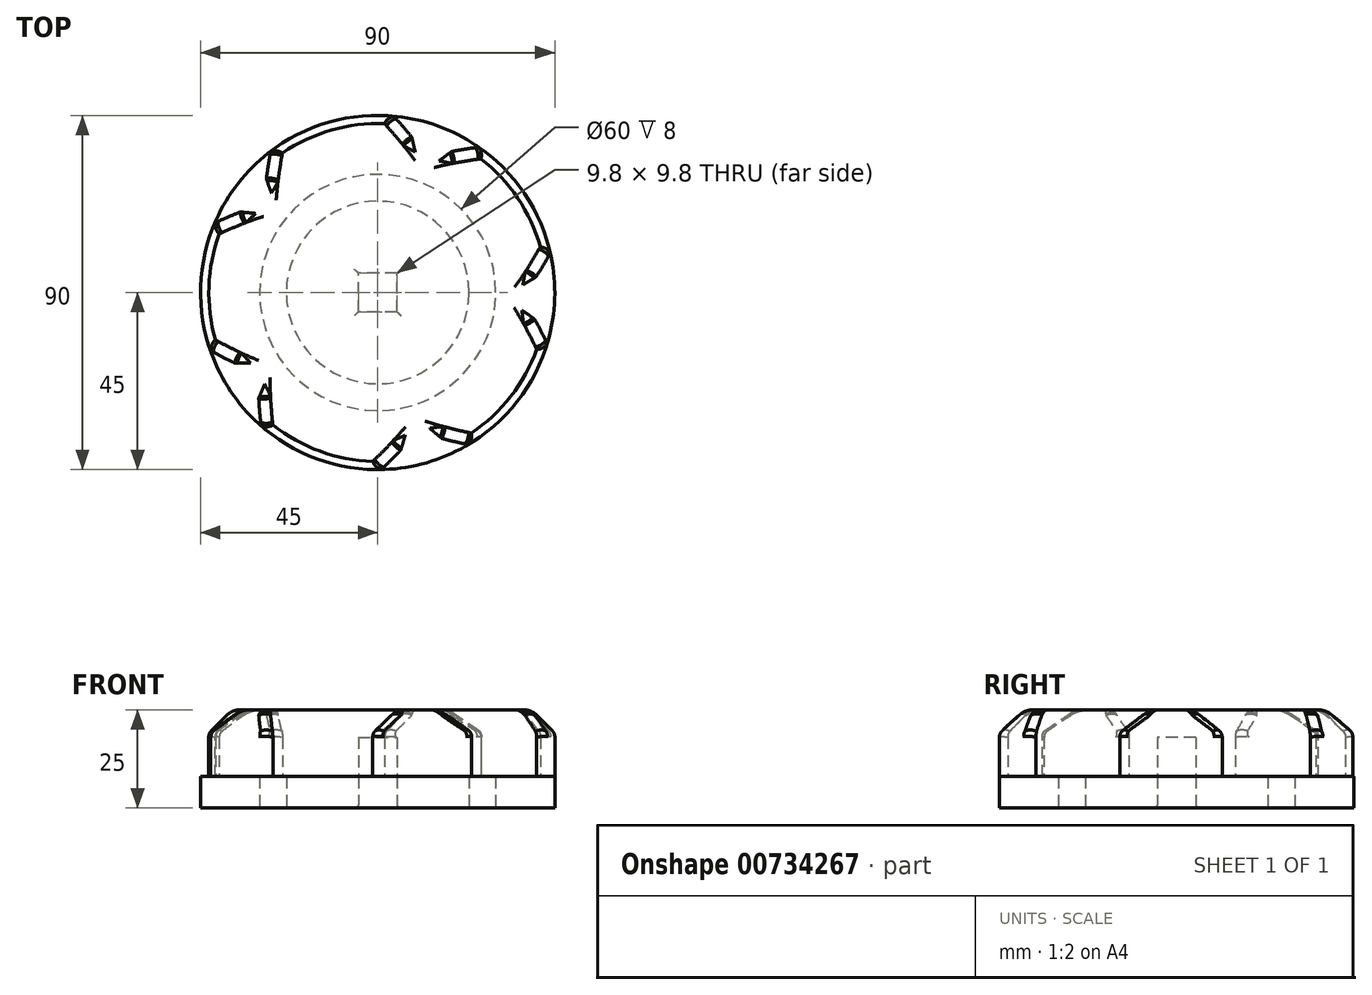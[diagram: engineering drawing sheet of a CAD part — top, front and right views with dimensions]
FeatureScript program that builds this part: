
annotation { "Feature Type Name" : "Feature", "Feature Type Description" : "" }
export const myFeature = defineFeature(function(context is Context, id is Id, definition is map)
    precondition{}
    {
        {
            var Q0;
            Q0=qCreatedBy(makeId("Top.planeOp"),FACE);
            var sketch = newSketch(context, id + "F0", { "sketchPlane" : qUnion([Q0])});
            skLineSegment(sketch, "E0.bottom", {"start": v(-4.9, 4.9) * mm, "end": v(4.9, 4.9) * mm});
            skLineSegment(sketch, "E0.top", {"start": v(-4.9, -4.9) * mm, "end": v(4.9, -4.9) * mm});
            skLineSegment(sketch, "E0.left", {"start": v(-4.9, 4.9) * mm, "end": v(-4.9, -4.9) * mm});
            skLineSegment(sketch, "E0.right", {"start": v(4.9, 4.9) * mm, "end": v(4.9, -4.9) * mm});
            skPoint(sketch, "E0.middle", {"position": v(0, 0) * mm});
            skCircle(sketch, "E1", {"center": v(0, 0) * mm, "radius": 23.2 * mm});
            skCircle(sketch, "E2", {"center": v(0, 0) * mm, "radius": 30 * mm});
            skCircle(sketch, "E3", {"center": v(0, 0) * mm, "radius": 45 * mm});
            skSolve(sketch);
        }
        {
            var Q0;
            Q0=makeQuery(id+"F0.imprint","IMPRINT",FACE,{"disambiguationData":[TD([[makeQuery(id+"F0.imprint","IMPRINT",EDGE,{"derivedFrom":sQuery(id+"F0.wireOp",EDGE,"E2")}),-1.0]])]});
            var Q1;
            Q1=makeQuery(id+"F0.imprint","IMPRINT",FACE,{"disambiguationData":[TD([[makeQuery(id+"F0.imprint","IMPRINT",EDGE,{"derivedFrom":sQuery(id+"F0.wireOp",EDGE,"E0.bottom")}),1.0]])]});
            extrude(context, id + "F1", {"entities" : qUnion([Q0, Q1]), "depth" : 8 * mm, "offsetDistance" : 25 * mm});
        }
        {
            var Q0;
            Q0=makeQuery(id+"F1.opExtrude","CAP_FACE",FACE,{"disambiguationData":[OSD([sQuery(id+"F0.wireOp",EDGE,"E2"),sQuery(id+"F0.wireOp",EDGE,"E3")])],"isStart":false});
            var sketch = newSketch(context, id + "F2", { "sketchPlane" : qUnion([Q0])});
            skArc(sketch, "E4", {"start": v(-42.2, 15.64) * mm, "mid": v(-44.97, 1.58) * mm, "end": v(-43.19, -12.65) * mm});
            skArc(sketch, "E5.1.1", {"start": v(-27.91, -35.3) * mm, "mid": v(-15.4, -42.28) * mm, "end": v(-1.32, -44.98) * mm});
            skArc(sketch, "E5.2.1", {"start": v(24.94, -37.45) * mm, "mid": v(35.46, -27.7) * mm, "end": v(42.37, -15.15) * mm});
            skArc(sketch, "E5.3.1", {"start": v(43.33, 12.15) * mm, "mid": v(37.3, 25.16) * mm, "end": v(27.5, 35.62) * mm});
            skArc(sketch, "E5.4.1", {"start": v(1.83, 44.96) * mm, "mid": v(-12.4, 43.26) * mm, "end": v(-25.37, 37.17) * mm});
            skCircle(sketch, "E6", {"center": v(0, 0) * mm, "radius": 45 * mm});
            skArc(sketch, "E7", {"start": v(-40.23, 14.91) * mm, "mid": v(-42.88, 1.5) * mm, "end": v(-41.18, -12.06) * mm});
            skLineSegment(sketch, "E8", {"start": v(-40.23, 14.91) * mm, "end": v(-42.2, 15.64) * mm});
            skLineSegment(sketch, "E9", {"start": v(-41.18, -12.06) * mm, "end": v(-43.19, -12.65) * mm});
            skLineSegment(sketch, "E10.1.0", {"start": v(-26.62, -33.66) * mm, "end": v(-27.91, -35.3) * mm});
            skArc(sketch, "E10.1.1", {"start": v(-26.62, -33.66) * mm, "mid": v(-14.68, -40.32) * mm, "end": v(-1.26, -42.9) * mm});
            skLineSegment(sketch, "E10.1.2", {"start": v(-1.26, -42.9) * mm, "end": v(-1.32, -44.98) * mm});
            skLineSegment(sketch, "E10.2.0", {"start": v(23.79, -35.71) * mm, "end": v(24.94, -37.45) * mm});
            skArc(sketch, "E10.2.1", {"start": v(23.79, -35.71) * mm, "mid": v(33.8, -26.42) * mm, "end": v(40.4, -14.45) * mm});
            skLineSegment(sketch, "E10.2.2", {"start": v(40.4, -14.45) * mm, "end": v(42.37, -15.15) * mm});
            skLineSegment(sketch, "E10.3.0", {"start": v(41.32, 11.58) * mm, "end": v(43.33, 12.15) * mm});
            skArc(sketch, "E10.3.1", {"start": v(41.32, 11.58) * mm, "mid": v(35.58, 23.99) * mm, "end": v(26.23, 33.96) * mm});
            skLineSegment(sketch, "E10.3.2", {"start": v(26.23, 33.96) * mm, "end": v(27.5, 35.62) * mm});
            skLineSegment(sketch, "E10.4.0", {"start": v(1.75, 42.87) * mm, "end": v(1.83, 44.96) * mm});
            skArc(sketch, "E10.4.1", {"start": v(1.75, 42.87) * mm, "mid": v(-11.82, 41.25) * mm, "end": v(-24.2, 35.44) * mm});
            skLineSegment(sketch, "E10.4.2", {"start": v(-24.2, 35.44) * mm, "end": v(-25.37, 37.17) * mm});
            skSolve(sketch);
        }
        {
            var Q0;
            Q0=makeQuery(id+"F2.imprint","IMPRINT",FACE,{"disambiguationData":[TD([[makeQuery(id+"F2.imprint","IMPRINT",EDGE,{"derivedFrom":sQuery(id+"F2.wireOp",EDGE,"E7")}),1.0]])]});
            var Q1;
            Q1=makeQuery(id+"F2.imprint","IMPRINT",FACE,{"disambiguationData":[TD([[makeQuery(id+"F2.imprint","IMPRINT",EDGE,{"derivedFrom":makeQuery(id+"F1.opExtrude","CAP_EDGE",EDGE,{"disambiguationData":[OSD([sQuery(id+"F0.wireOp",EDGE,"E2")])],"isStart":false})}),1.0]])]});
            extrude(context, id + "F3", {"entities" : qUnion([Q0, Q1]), "depth" : 17 * mm, "offsetDistance" : 25 * mm});
        }
        {
            var Q0;
            Q0=makeQuery(id+"F3.opExtrude","CAP_FACE",FACE,{"disambiguationData":[OSD([sQuery(id+"F2.wireOp",EDGE,"E6"),sQuery(id+"F2.wireOp",EDGE,"E7"),sQuery(id+"F2.wireOp",EDGE,"E8"),sQuery(id+"F2.wireOp",EDGE,"E9"),sQuery(id+"F2.wireOp",EDGE,"E10.1.0"),sQuery(id+"F2.wireOp",EDGE,"E10.1.1"),sQuery(id+"F2.wireOp",EDGE,"E10.1.2"),sQuery(id+"F2.wireOp",EDGE,"E10.2.0"),sQuery(id+"F2.wireOp",EDGE,"E10.2.1"),sQuery(id+"F2.wireOp",EDGE,"E10.2.2"),sQuery(id+"F2.wireOp",EDGE,"E10.3.0"),sQuery(id+"F2.wireOp",EDGE,"E10.3.1"),sQuery(id+"F2.wireOp",EDGE,"E10.3.2"),sQuery(id+"F2.wireOp",EDGE,"E10.4.0"),sQuery(id+"F2.wireOp",EDGE,"E10.4.1"),sQuery(id+"F2.wireOp",EDGE,"E10.4.2")])],"isStart":false});
            chamfer(context, id + "F4", {"entities" : qUnion([Q0]), "width" : 6 * mm, "tangentPropagation" : true});
        }
        {
            var Q0;
            Q0=makeQuery(id+"F3.opExtrude","CAP_FACE",FACE,{"disambiguationData":[OSD([sQuery(id+"F2.wireOp",EDGE,"E6"),sQuery(id+"F2.wireOp",EDGE,"E7"),sQuery(id+"F2.wireOp",EDGE,"E8"),sQuery(id+"F2.wireOp",EDGE,"E9"),sQuery(id+"F2.wireOp",EDGE,"E10.1.0"),sQuery(id+"F2.wireOp",EDGE,"E10.1.1"),sQuery(id+"F2.wireOp",EDGE,"E10.1.2"),sQuery(id+"F2.wireOp",EDGE,"E10.2.0"),sQuery(id+"F2.wireOp",EDGE,"E10.2.1"),sQuery(id+"F2.wireOp",EDGE,"E10.2.2"),sQuery(id+"F2.wireOp",EDGE,"E10.3.0"),sQuery(id+"F2.wireOp",EDGE,"E10.3.1"),sQuery(id+"F2.wireOp",EDGE,"E10.3.2"),sQuery(id+"F2.wireOp",EDGE,"E10.4.0"),sQuery(id+"F2.wireOp",EDGE,"E10.4.1"),sQuery(id+"F2.wireOp",EDGE,"E10.4.2")])],"isStart":false});
            fillet(context, id + "F5", {"entities" : qUnion([Q0]), "radius" : 5 * mm, "tangentPropagation" : true, "allowEdgeOverflow" : false});
        }
        {
            var Q0;
            Q0=makeQuery(id+"F3.opExtrude","SWEPT_EDGE",EDGE,{"disambiguationData":[OSD([sQuery(id+"F2.wireOp",EDGE,"E6"),sQuery(id+"F2.wireOp",EDGE,"E10.4.0")])]});
            var Q1;
            {var subQ0=sQuery(id+"F2.wireOp",EDGE,"E10.4.0");var subQ1=sQuery(id+"F2.wireOp",EDGE,"E6");Q1=makeQuery(id+"F4.opChamfer","BLEND_EDGE",EDGE,{"blendedFrom":[makeQuery(id+"F3.opExtrude","CAP_EDGE",EDGE,{"disambiguationData":[OSD([subQ1]),TDD([makeQuery(id+"F2.imprint","IMPRINT",EDGE,{"disambiguationData":[TD([[makeQuery(id+"F2.imprint","INTERSECT",VERTEX,{"derivedFrom":[subQ1,sQuery(id+"F2.wireOp",EDGE,"E10.3.2")]}),-1.0]])],"derivedFrom":subQ1})])],"isStart":false}),makeQuery(id+"F3.opExtrude","CAP_EDGE",EDGE,{"disambiguationData":[OSD([subQ0])],"isStart":false})],"blendedInto":[]});}
            var Q2;
            {var subQ0=sQuery(id+"F2.wireOp",EDGE,"E10.4.0");var subQ1=sQuery(id+"F2.wireOp",EDGE,"E10.3.2");var subQ2=sQuery(id+"F2.wireOp",EDGE,"E6");var subQ3=makeQuery(id+"F3.opExtrude","CAP_FACE",FACE,{"disambiguationData":[OSD([subQ2,sQuery(id+"F2.wireOp",EDGE,"E7"),sQuery(id+"F2.wireOp",EDGE,"E8"),sQuery(id+"F2.wireOp",EDGE,"E9"),sQuery(id+"F2.wireOp",EDGE,"E10.1.0"),sQuery(id+"F2.wireOp",EDGE,"E10.1.1"),sQuery(id+"F2.wireOp",EDGE,"E10.1.2"),sQuery(id+"F2.wireOp",EDGE,"E10.2.0"),sQuery(id+"F2.wireOp",EDGE,"E10.2.1"),sQuery(id+"F2.wireOp",EDGE,"E10.2.2"),sQuery(id+"F2.wireOp",EDGE,"E10.3.0"),sQuery(id+"F2.wireOp",EDGE,"E10.3.1"),subQ1,subQ0,sQuery(id+"F2.wireOp",EDGE,"E10.4.1"),sQuery(id+"F2.wireOp",EDGE,"E10.4.2")])],"isStart":false});Q2=makeQuery(id+"F5.opFillet","BLEND_EDGE",EDGE,{"blendedFrom":[makeQuery(id+"F4.opChamfer","BLEND_EDGE",EDGE,{"blendedFrom":[makeQuery(id+"F3.opExtrude","CAP_EDGE",EDGE,{"disambiguationData":[OSD([subQ2]),TDD([makeQuery(id+"F2.imprint","IMPRINT",EDGE,{"disambiguationData":[TD([[makeQuery(id+"F2.imprint","INTERSECT",VERTEX,{"derivedFrom":[subQ2,subQ1]}),-1.0]])],"derivedFrom":subQ2})])],"isStart":false}),subQ3],"blendedInto":[subQ3]}),makeQuery(id+"F4.opChamfer","BLEND_EDGE",EDGE,{"blendedFrom":[makeQuery(id+"F3.opExtrude","CAP_EDGE",EDGE,{"disambiguationData":[OSD([subQ0])],"isStart":false}),subQ3],"blendedInto":[subQ3]})],"blendedInto":[]});}
            var Q3;
            Q3=makeQuery(id+"F3.opExtrude","SWEPT_EDGE",EDGE,{"disambiguationData":[OSD([sQuery(id+"F2.wireOp",EDGE,"E6"),sQuery(id+"F2.wireOp",EDGE,"E10.4.2")])]});
            var Q4;
            {var subQ0=sQuery(id+"F2.wireOp",EDGE,"E10.4.2");var subQ1=sQuery(id+"F2.wireOp",EDGE,"E6");Q4=makeQuery(id+"F4.opChamfer","BLEND_EDGE",EDGE,{"blendedFrom":[makeQuery(id+"F3.opExtrude","CAP_EDGE",EDGE,{"disambiguationData":[OSD([subQ1]),TDD([makeQuery(id+"F2.imprint","IMPRINT",EDGE,{"disambiguationData":[TD([[makeQuery(id+"F2.imprint","INTERSECT",VERTEX,{"derivedFrom":[subQ1,sQuery(id+"F2.wireOp",EDGE,"E8")]}),1.0]])],"derivedFrom":subQ1})])],"isStart":false}),makeQuery(id+"F3.opExtrude","CAP_EDGE",EDGE,{"disambiguationData":[OSD([subQ0])],"isStart":false})],"blendedInto":[]});}
            var Q5;
            {var subQ0=sQuery(id+"F2.wireOp",EDGE,"E10.4.2");var subQ1=sQuery(id+"F2.wireOp",EDGE,"E8");var subQ2=sQuery(id+"F2.wireOp",EDGE,"E6");var subQ3=makeQuery(id+"F3.opExtrude","CAP_FACE",FACE,{"disambiguationData":[OSD([subQ2,sQuery(id+"F2.wireOp",EDGE,"E7"),subQ1,sQuery(id+"F2.wireOp",EDGE,"E9"),sQuery(id+"F2.wireOp",EDGE,"E10.1.0"),sQuery(id+"F2.wireOp",EDGE,"E10.1.1"),sQuery(id+"F2.wireOp",EDGE,"E10.1.2"),sQuery(id+"F2.wireOp",EDGE,"E10.2.0"),sQuery(id+"F2.wireOp",EDGE,"E10.2.1"),sQuery(id+"F2.wireOp",EDGE,"E10.2.2"),sQuery(id+"F2.wireOp",EDGE,"E10.3.0"),sQuery(id+"F2.wireOp",EDGE,"E10.3.1"),sQuery(id+"F2.wireOp",EDGE,"E10.3.2"),sQuery(id+"F2.wireOp",EDGE,"E10.4.0"),sQuery(id+"F2.wireOp",EDGE,"E10.4.1"),subQ0])],"isStart":false});Q5=makeQuery(id+"F5.opFillet","BLEND_EDGE",EDGE,{"blendedFrom":[makeQuery(id+"F4.opChamfer","BLEND_EDGE",EDGE,{"blendedFrom":[makeQuery(id+"F3.opExtrude","CAP_EDGE",EDGE,{"disambiguationData":[OSD([subQ2]),TDD([makeQuery(id+"F2.imprint","IMPRINT",EDGE,{"disambiguationData":[TD([[makeQuery(id+"F2.imprint","INTERSECT",VERTEX,{"derivedFrom":[subQ2,subQ1]}),1.0]])],"derivedFrom":subQ2})])],"isStart":false}),subQ3],"blendedInto":[subQ3]}),makeQuery(id+"F4.opChamfer","BLEND_EDGE",EDGE,{"blendedFrom":[makeQuery(id+"F3.opExtrude","CAP_EDGE",EDGE,{"disambiguationData":[OSD([subQ0])],"isStart":false}),subQ3],"blendedInto":[subQ3]})],"blendedInto":[]});}
            var Q6;
            Q6=makeQuery(id+"F3.opExtrude","SWEPT_EDGE",EDGE,{"disambiguationData":[OSD([sQuery(id+"F2.wireOp",EDGE,"E6"),sQuery(id+"F2.wireOp",EDGE,"E8")])]});
            var Q7;
            {var subQ0=sQuery(id+"F2.wireOp",EDGE,"E8");var subQ1=sQuery(id+"F2.wireOp",EDGE,"E6");Q7=makeQuery(id+"F4.opChamfer","BLEND_EDGE",EDGE,{"blendedFrom":[makeQuery(id+"F3.opExtrude","CAP_EDGE",EDGE,{"disambiguationData":[OSD([subQ1]),TDD([makeQuery(id+"F2.imprint","IMPRINT",EDGE,{"disambiguationData":[TD([[makeQuery(id+"F2.imprint","INTERSECT",VERTEX,{"derivedFrom":[subQ1,subQ0]}),1.0]])],"derivedFrom":subQ1})])],"isStart":false}),makeQuery(id+"F3.opExtrude","CAP_EDGE",EDGE,{"disambiguationData":[OSD([subQ0])],"isStart":false})],"blendedInto":[]});}
            var Q8;
            {var subQ0=sQuery(id+"F2.wireOp",EDGE,"E10.4.2");var subQ1=sQuery(id+"F2.wireOp",EDGE,"E8");var subQ2=sQuery(id+"F2.wireOp",EDGE,"E6");var subQ3=makeQuery(id+"F3.opExtrude","CAP_FACE",FACE,{"disambiguationData":[OSD([subQ2,sQuery(id+"F2.wireOp",EDGE,"E7"),subQ1,sQuery(id+"F2.wireOp",EDGE,"E9"),sQuery(id+"F2.wireOp",EDGE,"E10.1.0"),sQuery(id+"F2.wireOp",EDGE,"E10.1.1"),sQuery(id+"F2.wireOp",EDGE,"E10.1.2"),sQuery(id+"F2.wireOp",EDGE,"E10.2.0"),sQuery(id+"F2.wireOp",EDGE,"E10.2.1"),sQuery(id+"F2.wireOp",EDGE,"E10.2.2"),sQuery(id+"F2.wireOp",EDGE,"E10.3.0"),sQuery(id+"F2.wireOp",EDGE,"E10.3.1"),sQuery(id+"F2.wireOp",EDGE,"E10.3.2"),sQuery(id+"F2.wireOp",EDGE,"E10.4.0"),sQuery(id+"F2.wireOp",EDGE,"E10.4.1"),subQ0])],"isStart":false});Q8=makeQuery(id+"F5.opFillet","BLEND_EDGE",EDGE,{"blendedFrom":[makeQuery(id+"F4.opChamfer","BLEND_EDGE",EDGE,{"blendedFrom":[makeQuery(id+"F3.opExtrude","CAP_EDGE",EDGE,{"disambiguationData":[OSD([subQ2]),TDD([makeQuery(id+"F2.imprint","IMPRINT",EDGE,{"disambiguationData":[TD([[makeQuery(id+"F2.imprint","INTERSECT",VERTEX,{"derivedFrom":[subQ2,subQ1]}),1.0]])],"derivedFrom":subQ2})])],"isStart":false}),subQ3],"blendedInto":[subQ3]}),makeQuery(id+"F4.opChamfer","BLEND_EDGE",EDGE,{"blendedFrom":[makeQuery(id+"F3.opExtrude","CAP_EDGE",EDGE,{"disambiguationData":[OSD([subQ1])],"isStart":false}),subQ3],"blendedInto":[subQ3]})],"blendedInto":[]});}
            var Q9;
            {var subQ0=sQuery(id+"F2.wireOp",EDGE,"E9");var subQ1=sQuery(id+"F2.wireOp",EDGE,"E6");Q9=makeQuery(id+"F4.opChamfer","BLEND_EDGE",EDGE,{"blendedFrom":[makeQuery(id+"F3.opExtrude","CAP_EDGE",EDGE,{"disambiguationData":[OSD([subQ1]),TDD([makeQuery(id+"F2.imprint","IMPRINT",EDGE,{"disambiguationData":[TD([[makeQuery(id+"F2.imprint","INTERSECT",VERTEX,{"derivedFrom":[subQ1,subQ0]}),-1.0]])],"derivedFrom":subQ1})])],"isStart":false}),makeQuery(id+"F3.opExtrude","CAP_EDGE",EDGE,{"disambiguationData":[OSD([subQ0])],"isStart":false})],"blendedInto":[]});}
            var Q10;
            Q10=makeQuery(id+"F3.opExtrude","SWEPT_EDGE",EDGE,{"disambiguationData":[OSD([sQuery(id+"F2.wireOp",EDGE,"E6"),sQuery(id+"F2.wireOp",EDGE,"E9")])]});
            var Q11;
            {var subQ0=sQuery(id+"F2.wireOp",EDGE,"E10.1.0");var subQ1=sQuery(id+"F2.wireOp",EDGE,"E9");var subQ2=sQuery(id+"F2.wireOp",EDGE,"E6");var subQ3=makeQuery(id+"F3.opExtrude","CAP_FACE",FACE,{"disambiguationData":[OSD([subQ2,sQuery(id+"F2.wireOp",EDGE,"E7"),sQuery(id+"F2.wireOp",EDGE,"E8"),subQ1,subQ0,sQuery(id+"F2.wireOp",EDGE,"E10.1.1"),sQuery(id+"F2.wireOp",EDGE,"E10.1.2"),sQuery(id+"F2.wireOp",EDGE,"E10.2.0"),sQuery(id+"F2.wireOp",EDGE,"E10.2.1"),sQuery(id+"F2.wireOp",EDGE,"E10.2.2"),sQuery(id+"F2.wireOp",EDGE,"E10.3.0"),sQuery(id+"F2.wireOp",EDGE,"E10.3.1"),sQuery(id+"F2.wireOp",EDGE,"E10.3.2"),sQuery(id+"F2.wireOp",EDGE,"E10.4.0"),sQuery(id+"F2.wireOp",EDGE,"E10.4.1"),sQuery(id+"F2.wireOp",EDGE,"E10.4.2")])],"isStart":false});Q11=makeQuery(id+"F5.opFillet","BLEND_EDGE",EDGE,{"blendedFrom":[makeQuery(id+"F4.opChamfer","BLEND_EDGE",EDGE,{"blendedFrom":[makeQuery(id+"F3.opExtrude","CAP_EDGE",EDGE,{"disambiguationData":[OSD([subQ2]),TDD([makeQuery(id+"F2.imprint","IMPRINT",EDGE,{"disambiguationData":[TD([[makeQuery(id+"F2.imprint","INTERSECT",VERTEX,{"derivedFrom":[subQ2,subQ1]}),-1.0]])],"derivedFrom":subQ2})])],"isStart":false}),subQ3],"blendedInto":[subQ3]}),makeQuery(id+"F4.opChamfer","BLEND_EDGE",EDGE,{"blendedFrom":[makeQuery(id+"F3.opExtrude","CAP_EDGE",EDGE,{"disambiguationData":[OSD([subQ1])],"isStart":false}),subQ3],"blendedInto":[subQ3]})],"blendedInto":[]});}
            var Q12;
            {var subQ0=sQuery(id+"F2.wireOp",EDGE,"E10.1.0");var subQ1=sQuery(id+"F2.wireOp",EDGE,"E9");var subQ2=sQuery(id+"F2.wireOp",EDGE,"E6");var subQ3=makeQuery(id+"F3.opExtrude","CAP_FACE",FACE,{"disambiguationData":[OSD([subQ2,sQuery(id+"F2.wireOp",EDGE,"E7"),sQuery(id+"F2.wireOp",EDGE,"E8"),subQ1,subQ0,sQuery(id+"F2.wireOp",EDGE,"E10.1.1"),sQuery(id+"F2.wireOp",EDGE,"E10.1.2"),sQuery(id+"F2.wireOp",EDGE,"E10.2.0"),sQuery(id+"F2.wireOp",EDGE,"E10.2.1"),sQuery(id+"F2.wireOp",EDGE,"E10.2.2"),sQuery(id+"F2.wireOp",EDGE,"E10.3.0"),sQuery(id+"F2.wireOp",EDGE,"E10.3.1"),sQuery(id+"F2.wireOp",EDGE,"E10.3.2"),sQuery(id+"F2.wireOp",EDGE,"E10.4.0"),sQuery(id+"F2.wireOp",EDGE,"E10.4.1"),sQuery(id+"F2.wireOp",EDGE,"E10.4.2")])],"isStart":false});Q12=makeQuery(id+"F5.opFillet","BLEND_EDGE",EDGE,{"blendedFrom":[makeQuery(id+"F4.opChamfer","BLEND_EDGE",EDGE,{"blendedFrom":[makeQuery(id+"F3.opExtrude","CAP_EDGE",EDGE,{"disambiguationData":[OSD([subQ2]),TDD([makeQuery(id+"F2.imprint","IMPRINT",EDGE,{"disambiguationData":[TD([[makeQuery(id+"F2.imprint","INTERSECT",VERTEX,{"derivedFrom":[subQ2,subQ1]}),-1.0]])],"derivedFrom":subQ2})])],"isStart":false}),subQ3],"blendedInto":[subQ3]}),makeQuery(id+"F4.opChamfer","BLEND_EDGE",EDGE,{"blendedFrom":[makeQuery(id+"F3.opExtrude","CAP_EDGE",EDGE,{"disambiguationData":[OSD([subQ0])],"isStart":false}),subQ3],"blendedInto":[subQ3]})],"blendedInto":[]});}
            var Q13;
            {var subQ0=sQuery(id+"F2.wireOp",EDGE,"E10.1.0");var subQ1=sQuery(id+"F2.wireOp",EDGE,"E6");Q13=makeQuery(id+"F4.opChamfer","BLEND_EDGE",EDGE,{"blendedFrom":[makeQuery(id+"F3.opExtrude","CAP_EDGE",EDGE,{"disambiguationData":[OSD([subQ1]),TDD([makeQuery(id+"F2.imprint","IMPRINT",EDGE,{"disambiguationData":[TD([[makeQuery(id+"F2.imprint","INTERSECT",VERTEX,{"derivedFrom":[subQ1,sQuery(id+"F2.wireOp",EDGE,"E9")]}),-1.0]])],"derivedFrom":subQ1})])],"isStart":false}),makeQuery(id+"F3.opExtrude","CAP_EDGE",EDGE,{"disambiguationData":[OSD([subQ0])],"isStart":false})],"blendedInto":[]});}
            var Q14;
            Q14=makeQuery(id+"F3.opExtrude","SWEPT_EDGE",EDGE,{"disambiguationData":[OSD([sQuery(id+"F2.wireOp",EDGE,"E6"),sQuery(id+"F2.wireOp",EDGE,"E10.1.0")])]});
            var Q15;
            Q15=makeQuery(id+"F3.opExtrude","SWEPT_EDGE",EDGE,{"disambiguationData":[OSD([sQuery(id+"F2.wireOp",EDGE,"E6"),sQuery(id+"F2.wireOp",EDGE,"E10.1.2")])]});
            var Q16;
            {var subQ0=sQuery(id+"F2.wireOp",EDGE,"E10.1.2");var subQ1=sQuery(id+"F2.wireOp",EDGE,"E6");Q16=makeQuery(id+"F4.opChamfer","BLEND_EDGE",EDGE,{"blendedFrom":[makeQuery(id+"F3.opExtrude","CAP_EDGE",EDGE,{"disambiguationData":[OSD([subQ1]),TDD([makeQuery(id+"F2.imprint","IMPRINT",EDGE,{"disambiguationData":[TD([[makeQuery(id+"F2.imprint","INTERSECT",VERTEX,{"derivedFrom":[subQ1,subQ0]}),-1.0]])],"derivedFrom":subQ1})])],"isStart":false}),makeQuery(id+"F3.opExtrude","CAP_EDGE",EDGE,{"disambiguationData":[OSD([subQ0])],"isStart":false})],"blendedInto":[]});}
            var Q17;
            {var subQ0=sQuery(id+"F2.wireOp",EDGE,"E10.2.0");var subQ1=sQuery(id+"F2.wireOp",EDGE,"E10.1.2");var subQ2=sQuery(id+"F2.wireOp",EDGE,"E6");var subQ3=makeQuery(id+"F3.opExtrude","CAP_FACE",FACE,{"disambiguationData":[OSD([subQ2,sQuery(id+"F2.wireOp",EDGE,"E7"),sQuery(id+"F2.wireOp",EDGE,"E8"),sQuery(id+"F2.wireOp",EDGE,"E9"),sQuery(id+"F2.wireOp",EDGE,"E10.1.0"),sQuery(id+"F2.wireOp",EDGE,"E10.1.1"),subQ1,subQ0,sQuery(id+"F2.wireOp",EDGE,"E10.2.1"),sQuery(id+"F2.wireOp",EDGE,"E10.2.2"),sQuery(id+"F2.wireOp",EDGE,"E10.3.0"),sQuery(id+"F2.wireOp",EDGE,"E10.3.1"),sQuery(id+"F2.wireOp",EDGE,"E10.3.2"),sQuery(id+"F2.wireOp",EDGE,"E10.4.0"),sQuery(id+"F2.wireOp",EDGE,"E10.4.1"),sQuery(id+"F2.wireOp",EDGE,"E10.4.2")])],"isStart":false});Q17=makeQuery(id+"F5.opFillet","BLEND_EDGE",EDGE,{"blendedFrom":[makeQuery(id+"F4.opChamfer","BLEND_EDGE",EDGE,{"blendedFrom":[makeQuery(id+"F3.opExtrude","CAP_EDGE",EDGE,{"disambiguationData":[OSD([subQ2]),TDD([makeQuery(id+"F2.imprint","IMPRINT",EDGE,{"disambiguationData":[TD([[makeQuery(id+"F2.imprint","INTERSECT",VERTEX,{"derivedFrom":[subQ2,subQ1]}),-1.0]])],"derivedFrom":subQ2})])],"isStart":false}),subQ3],"blendedInto":[subQ3]}),makeQuery(id+"F4.opChamfer","BLEND_EDGE",EDGE,{"blendedFrom":[makeQuery(id+"F3.opExtrude","CAP_EDGE",EDGE,{"disambiguationData":[OSD([subQ1])],"isStart":false}),subQ3],"blendedInto":[subQ3]})],"blendedInto":[]});}
            var Q18;
            {var subQ0=sQuery(id+"F2.wireOp",EDGE,"E10.2.0");var subQ1=sQuery(id+"F2.wireOp",EDGE,"E10.1.2");var subQ2=sQuery(id+"F2.wireOp",EDGE,"E6");var subQ3=makeQuery(id+"F3.opExtrude","CAP_FACE",FACE,{"disambiguationData":[OSD([subQ2,sQuery(id+"F2.wireOp",EDGE,"E7"),sQuery(id+"F2.wireOp",EDGE,"E8"),sQuery(id+"F2.wireOp",EDGE,"E9"),sQuery(id+"F2.wireOp",EDGE,"E10.1.0"),sQuery(id+"F2.wireOp",EDGE,"E10.1.1"),subQ1,subQ0,sQuery(id+"F2.wireOp",EDGE,"E10.2.1"),sQuery(id+"F2.wireOp",EDGE,"E10.2.2"),sQuery(id+"F2.wireOp",EDGE,"E10.3.0"),sQuery(id+"F2.wireOp",EDGE,"E10.3.1"),sQuery(id+"F2.wireOp",EDGE,"E10.3.2"),sQuery(id+"F2.wireOp",EDGE,"E10.4.0"),sQuery(id+"F2.wireOp",EDGE,"E10.4.1"),sQuery(id+"F2.wireOp",EDGE,"E10.4.2")])],"isStart":false});Q18=makeQuery(id+"F5.opFillet","BLEND_EDGE",EDGE,{"blendedFrom":[makeQuery(id+"F4.opChamfer","BLEND_EDGE",EDGE,{"blendedFrom":[makeQuery(id+"F3.opExtrude","CAP_EDGE",EDGE,{"disambiguationData":[OSD([subQ2]),TDD([makeQuery(id+"F2.imprint","IMPRINT",EDGE,{"disambiguationData":[TD([[makeQuery(id+"F2.imprint","INTERSECT",VERTEX,{"derivedFrom":[subQ2,subQ1]}),-1.0]])],"derivedFrom":subQ2})])],"isStart":false}),subQ3],"blendedInto":[subQ3]}),makeQuery(id+"F4.opChamfer","BLEND_EDGE",EDGE,{"blendedFrom":[makeQuery(id+"F3.opExtrude","CAP_EDGE",EDGE,{"disambiguationData":[OSD([subQ0])],"isStart":false}),subQ3],"blendedInto":[subQ3]})],"blendedInto":[]});}
            var Q19;
            {var subQ0=sQuery(id+"F2.wireOp",EDGE,"E10.2.0");var subQ1=sQuery(id+"F2.wireOp",EDGE,"E6");Q19=makeQuery(id+"F4.opChamfer","BLEND_EDGE",EDGE,{"blendedFrom":[makeQuery(id+"F3.opExtrude","CAP_EDGE",EDGE,{"disambiguationData":[OSD([subQ1]),TDD([makeQuery(id+"F2.imprint","IMPRINT",EDGE,{"disambiguationData":[TD([[makeQuery(id+"F2.imprint","INTERSECT",VERTEX,{"derivedFrom":[subQ1,sQuery(id+"F2.wireOp",EDGE,"E10.1.2")]}),-1.0]])],"derivedFrom":subQ1})])],"isStart":false}),makeQuery(id+"F3.opExtrude","CAP_EDGE",EDGE,{"disambiguationData":[OSD([subQ0])],"isStart":false})],"blendedInto":[]});}
            var Q20;
            Q20=makeQuery(id+"F3.opExtrude","SWEPT_EDGE",EDGE,{"disambiguationData":[OSD([sQuery(id+"F2.wireOp",EDGE,"E6"),sQuery(id+"F2.wireOp",EDGE,"E10.2.0")])]});
            var Q21;
            Q21=makeQuery(id+"F3.opExtrude","SWEPT_EDGE",EDGE,{"disambiguationData":[OSD([sQuery(id+"F2.wireOp",EDGE,"E6"),sQuery(id+"F2.wireOp",EDGE,"E10.2.2")])]});
            var Q22;
            {var subQ0=sQuery(id+"F2.wireOp",EDGE,"E10.2.2");var subQ1=sQuery(id+"F2.wireOp",EDGE,"E6");Q22=makeQuery(id+"F4.opChamfer","BLEND_EDGE",EDGE,{"blendedFrom":[makeQuery(id+"F3.opExtrude","CAP_EDGE",EDGE,{"disambiguationData":[OSD([subQ1]),TDD([makeQuery(id+"F2.imprint","IMPRINT",EDGE,{"disambiguationData":[TD([[makeQuery(id+"F2.imprint","INTERSECT",VERTEX,{"derivedFrom":[subQ1,subQ0]}),-1.0]])],"derivedFrom":subQ1})])],"isStart":false}),makeQuery(id+"F3.opExtrude","CAP_EDGE",EDGE,{"disambiguationData":[OSD([subQ0])],"isStart":false})],"blendedInto":[]});}
            var Q23;
            {var subQ0=sQuery(id+"F2.wireOp",EDGE,"E10.3.0");var subQ1=sQuery(id+"F2.wireOp",EDGE,"E10.2.2");var subQ2=sQuery(id+"F2.wireOp",EDGE,"E6");var subQ3=makeQuery(id+"F3.opExtrude","CAP_FACE",FACE,{"disambiguationData":[OSD([subQ2,sQuery(id+"F2.wireOp",EDGE,"E7"),sQuery(id+"F2.wireOp",EDGE,"E8"),sQuery(id+"F2.wireOp",EDGE,"E9"),sQuery(id+"F2.wireOp",EDGE,"E10.1.0"),sQuery(id+"F2.wireOp",EDGE,"E10.1.1"),sQuery(id+"F2.wireOp",EDGE,"E10.1.2"),sQuery(id+"F2.wireOp",EDGE,"E10.2.0"),sQuery(id+"F2.wireOp",EDGE,"E10.2.1"),subQ1,subQ0,sQuery(id+"F2.wireOp",EDGE,"E10.3.1"),sQuery(id+"F2.wireOp",EDGE,"E10.3.2"),sQuery(id+"F2.wireOp",EDGE,"E10.4.0"),sQuery(id+"F2.wireOp",EDGE,"E10.4.1"),sQuery(id+"F2.wireOp",EDGE,"E10.4.2")])],"isStart":false});Q23=makeQuery(id+"F5.opFillet","BLEND_EDGE",EDGE,{"blendedFrom":[makeQuery(id+"F4.opChamfer","BLEND_EDGE",EDGE,{"blendedFrom":[makeQuery(id+"F3.opExtrude","CAP_EDGE",EDGE,{"disambiguationData":[OSD([subQ2]),TDD([makeQuery(id+"F2.imprint","IMPRINT",EDGE,{"disambiguationData":[TD([[makeQuery(id+"F2.imprint","INTERSECT",VERTEX,{"derivedFrom":[subQ2,subQ1]}),-1.0]])],"derivedFrom":subQ2})])],"isStart":false}),subQ3],"blendedInto":[subQ3]}),makeQuery(id+"F4.opChamfer","BLEND_EDGE",EDGE,{"blendedFrom":[makeQuery(id+"F3.opExtrude","CAP_EDGE",EDGE,{"disambiguationData":[OSD([subQ1])],"isStart":false}),subQ3],"blendedInto":[subQ3]})],"blendedInto":[]});}
            var Q24;
            Q24=makeQuery(id+"F3.opExtrude","SWEPT_EDGE",EDGE,{"disambiguationData":[OSD([sQuery(id+"F2.wireOp",EDGE,"E6"),sQuery(id+"F2.wireOp",EDGE,"E10.3.0")])]});
            var Q25;
            {var subQ0=sQuery(id+"F2.wireOp",EDGE,"E10.3.0");var subQ1=sQuery(id+"F2.wireOp",EDGE,"E6");Q25=makeQuery(id+"F4.opChamfer","BLEND_EDGE",EDGE,{"blendedFrom":[makeQuery(id+"F3.opExtrude","CAP_EDGE",EDGE,{"disambiguationData":[OSD([subQ1]),TDD([makeQuery(id+"F2.imprint","IMPRINT",EDGE,{"disambiguationData":[TD([[makeQuery(id+"F2.imprint","INTERSECT",VERTEX,{"derivedFrom":[subQ1,sQuery(id+"F2.wireOp",EDGE,"E10.2.2")]}),-1.0]])],"derivedFrom":subQ1})])],"isStart":false}),makeQuery(id+"F3.opExtrude","CAP_EDGE",EDGE,{"disambiguationData":[OSD([subQ0])],"isStart":false})],"blendedInto":[]});}
            var Q26;
            {var subQ0=sQuery(id+"F2.wireOp",EDGE,"E10.3.0");var subQ1=sQuery(id+"F2.wireOp",EDGE,"E10.2.2");var subQ2=sQuery(id+"F2.wireOp",EDGE,"E6");var subQ3=makeQuery(id+"F3.opExtrude","CAP_FACE",FACE,{"disambiguationData":[OSD([subQ2,sQuery(id+"F2.wireOp",EDGE,"E7"),sQuery(id+"F2.wireOp",EDGE,"E8"),sQuery(id+"F2.wireOp",EDGE,"E9"),sQuery(id+"F2.wireOp",EDGE,"E10.1.0"),sQuery(id+"F2.wireOp",EDGE,"E10.1.1"),sQuery(id+"F2.wireOp",EDGE,"E10.1.2"),sQuery(id+"F2.wireOp",EDGE,"E10.2.0"),sQuery(id+"F2.wireOp",EDGE,"E10.2.1"),subQ1,subQ0,sQuery(id+"F2.wireOp",EDGE,"E10.3.1"),sQuery(id+"F2.wireOp",EDGE,"E10.3.2"),sQuery(id+"F2.wireOp",EDGE,"E10.4.0"),sQuery(id+"F2.wireOp",EDGE,"E10.4.1"),sQuery(id+"F2.wireOp",EDGE,"E10.4.2")])],"isStart":false});Q26=makeQuery(id+"F5.opFillet","BLEND_EDGE",EDGE,{"blendedFrom":[makeQuery(id+"F4.opChamfer","BLEND_EDGE",EDGE,{"blendedFrom":[makeQuery(id+"F3.opExtrude","CAP_EDGE",EDGE,{"disambiguationData":[OSD([subQ2]),TDD([makeQuery(id+"F2.imprint","IMPRINT",EDGE,{"disambiguationData":[TD([[makeQuery(id+"F2.imprint","INTERSECT",VERTEX,{"derivedFrom":[subQ2,subQ1]}),-1.0]])],"derivedFrom":subQ2})])],"isStart":false}),subQ3],"blendedInto":[subQ3]}),makeQuery(id+"F4.opChamfer","BLEND_EDGE",EDGE,{"blendedFrom":[makeQuery(id+"F3.opExtrude","CAP_EDGE",EDGE,{"disambiguationData":[OSD([subQ0])],"isStart":false}),subQ3],"blendedInto":[subQ3]})],"blendedInto":[]});}
            var Q27;
            Q27=makeQuery(id+"F3.opExtrude","SWEPT_EDGE",EDGE,{"disambiguationData":[OSD([sQuery(id+"F2.wireOp",EDGE,"E6"),sQuery(id+"F2.wireOp",EDGE,"E10.3.2")])]});
            var Q28;
            {var subQ0=sQuery(id+"F2.wireOp",EDGE,"E10.3.2");var subQ1=sQuery(id+"F2.wireOp",EDGE,"E6");Q28=makeQuery(id+"F4.opChamfer","BLEND_EDGE",EDGE,{"blendedFrom":[makeQuery(id+"F3.opExtrude","CAP_EDGE",EDGE,{"disambiguationData":[OSD([subQ1]),TDD([makeQuery(id+"F2.imprint","IMPRINT",EDGE,{"disambiguationData":[TD([[makeQuery(id+"F2.imprint","INTERSECT",VERTEX,{"derivedFrom":[subQ1,subQ0]}),-1.0]])],"derivedFrom":subQ1})])],"isStart":false}),makeQuery(id+"F3.opExtrude","CAP_EDGE",EDGE,{"disambiguationData":[OSD([subQ0])],"isStart":false})],"blendedInto":[]});}
            var Q29;
            {var subQ0=sQuery(id+"F2.wireOp",EDGE,"E10.4.0");var subQ1=sQuery(id+"F2.wireOp",EDGE,"E10.3.2");var subQ2=sQuery(id+"F2.wireOp",EDGE,"E6");var subQ3=makeQuery(id+"F3.opExtrude","CAP_FACE",FACE,{"disambiguationData":[OSD([subQ2,sQuery(id+"F2.wireOp",EDGE,"E7"),sQuery(id+"F2.wireOp",EDGE,"E8"),sQuery(id+"F2.wireOp",EDGE,"E9"),sQuery(id+"F2.wireOp",EDGE,"E10.1.0"),sQuery(id+"F2.wireOp",EDGE,"E10.1.1"),sQuery(id+"F2.wireOp",EDGE,"E10.1.2"),sQuery(id+"F2.wireOp",EDGE,"E10.2.0"),sQuery(id+"F2.wireOp",EDGE,"E10.2.1"),sQuery(id+"F2.wireOp",EDGE,"E10.2.2"),sQuery(id+"F2.wireOp",EDGE,"E10.3.0"),sQuery(id+"F2.wireOp",EDGE,"E10.3.1"),subQ1,subQ0,sQuery(id+"F2.wireOp",EDGE,"E10.4.1"),sQuery(id+"F2.wireOp",EDGE,"E10.4.2")])],"isStart":false});Q29=makeQuery(id+"F5.opFillet","BLEND_EDGE",EDGE,{"blendedFrom":[makeQuery(id+"F4.opChamfer","BLEND_EDGE",EDGE,{"blendedFrom":[makeQuery(id+"F3.opExtrude","CAP_EDGE",EDGE,{"disambiguationData":[OSD([subQ2]),TDD([makeQuery(id+"F2.imprint","IMPRINT",EDGE,{"disambiguationData":[TD([[makeQuery(id+"F2.imprint","INTERSECT",VERTEX,{"derivedFrom":[subQ2,subQ1]}),-1.0]])],"derivedFrom":subQ2})])],"isStart":false}),subQ3],"blendedInto":[subQ3]}),makeQuery(id+"F4.opChamfer","BLEND_EDGE",EDGE,{"blendedFrom":[makeQuery(id+"F3.opExtrude","CAP_EDGE",EDGE,{"disambiguationData":[OSD([subQ1])],"isStart":false}),subQ3],"blendedInto":[subQ3]})],"blendedInto":[]});}
            fillet(context, id + "F6", {"entities" : qUnion([Q0, Q1, Q2, Q3, Q4, Q5, Q6, Q7, Q8, Q9, Q10, Q11, Q12, Q13, Q14, Q15, Q16, Q17, Q18, Q19, Q20, Q21, Q22, Q23, Q24, Q25, Q26, Q27, Q28, Q29]), "radius" : 3 * mm, "tangentPropagation" : true, "allowEdgeOverflow" : false});
        }
        {
            var Q0;
            {var subQ0=sQuery(id+"F2.wireOp",EDGE,"E6");var subQ1=makeQuery(id+"F2.imprint","IMPRINT",EDGE,{"disambiguationData":[TD([[makeQuery(id+"F2.imprint","INTERSECT",VERTEX,{"derivedFrom":[subQ0,sQuery(id+"F2.wireOp",EDGE,"E10.1.2")]}),-1.0]])],"derivedFrom":subQ0});Q0=makeQuery(id+"F4.opChamfer","BLEND_EDGE",EDGE,{"blendedFrom":[makeQuery(id+"F3.opExtrude","CAP_EDGE",EDGE,{"disambiguationData":[OSD([subQ0]),TDD([subQ1])],"isStart":false}),makeQuery(id+"F3.opExtrude","SWEPT_FACE",FACE,{"disambiguationData":[OSD([subQ0]),TDD([subQ1])]})],"blendedInto":[makeQuery(id+"F3.opExtrude","SWEPT_FACE",FACE,{"disambiguationData":[OSD([subQ0]),TDD([subQ1])]})]});}
            var Q1;
            {var subQ0=sQuery(id+"F2.wireOp",EDGE,"E10.2.1");Q1=makeQuery(id+"F4.opChamfer","BLEND_EDGE",EDGE,{"blendedFrom":[makeQuery(id+"F3.opExtrude","CAP_EDGE",EDGE,{"disambiguationData":[OSD([subQ0])],"isStart":false}),makeQuery(id+"F3.opExtrude","SWEPT_FACE",FACE,{"disambiguationData":[OSD([subQ0])]})],"blendedInto":[makeQuery(id+"F3.opExtrude","SWEPT_FACE",FACE,{"disambiguationData":[OSD([subQ0])]})]});}
            var Q2;
            {var subQ0=sQuery(id+"F2.wireOp",EDGE,"E10.1.1");Q2=makeQuery(id+"F4.opChamfer","BLEND_EDGE",EDGE,{"blendedFrom":[makeQuery(id+"F3.opExtrude","CAP_EDGE",EDGE,{"disambiguationData":[OSD([subQ0])],"isStart":false}),makeQuery(id+"F3.opExtrude","SWEPT_FACE",FACE,{"disambiguationData":[OSD([subQ0])]})],"blendedInto":[makeQuery(id+"F3.opExtrude","SWEPT_FACE",FACE,{"disambiguationData":[OSD([subQ0])]})]});}
            var Q3;
            {var subQ0=sQuery(id+"F2.wireOp",EDGE,"E6");var subQ1=makeQuery(id+"F2.imprint","IMPRINT",EDGE,{"disambiguationData":[TD([[makeQuery(id+"F2.imprint","INTERSECT",VERTEX,{"derivedFrom":[subQ0,sQuery(id+"F2.wireOp",EDGE,"E9")]}),-1.0]])],"derivedFrom":subQ0});Q3=makeQuery(id+"F4.opChamfer","BLEND_EDGE",EDGE,{"blendedFrom":[makeQuery(id+"F3.opExtrude","CAP_EDGE",EDGE,{"disambiguationData":[OSD([subQ0]),TDD([subQ1])],"isStart":false}),makeQuery(id+"F3.opExtrude","SWEPT_FACE",FACE,{"disambiguationData":[OSD([subQ0]),TDD([subQ1])]})],"blendedInto":[makeQuery(id+"F3.opExtrude","SWEPT_FACE",FACE,{"disambiguationData":[OSD([subQ0]),TDD([subQ1])]})]});}
            var Q4;
            {var subQ0=sQuery(id+"F2.wireOp",EDGE,"E7");Q4=makeQuery(id+"F4.opChamfer","BLEND_EDGE",EDGE,{"blendedFrom":[makeQuery(id+"F3.opExtrude","CAP_EDGE",EDGE,{"disambiguationData":[OSD([subQ0])],"isStart":false}),makeQuery(id+"F3.opExtrude","SWEPT_FACE",FACE,{"disambiguationData":[OSD([subQ0])]})],"blendedInto":[makeQuery(id+"F3.opExtrude","SWEPT_FACE",FACE,{"disambiguationData":[OSD([subQ0])]})]});}
            var Q5;
            {var subQ0=sQuery(id+"F2.wireOp",EDGE,"E6");var subQ1=makeQuery(id+"F2.imprint","IMPRINT",EDGE,{"disambiguationData":[TD([[makeQuery(id+"F2.imprint","INTERSECT",VERTEX,{"derivedFrom":[subQ0,sQuery(id+"F2.wireOp",EDGE,"E8")]}),1.0]])],"derivedFrom":subQ0});Q5=makeQuery(id+"F4.opChamfer","BLEND_EDGE",EDGE,{"blendedFrom":[makeQuery(id+"F3.opExtrude","CAP_EDGE",EDGE,{"disambiguationData":[OSD([subQ0]),TDD([subQ1])],"isStart":false}),makeQuery(id+"F3.opExtrude","SWEPT_FACE",FACE,{"disambiguationData":[OSD([subQ0]),TDD([subQ1])]})],"blendedInto":[makeQuery(id+"F3.opExtrude","SWEPT_FACE",FACE,{"disambiguationData":[OSD([subQ0]),TDD([subQ1])]})]});}
            var Q6;
            {var subQ0=sQuery(id+"F2.wireOp",EDGE,"E10.4.1");Q6=makeQuery(id+"F4.opChamfer","BLEND_EDGE",EDGE,{"blendedFrom":[makeQuery(id+"F3.opExtrude","CAP_EDGE",EDGE,{"disambiguationData":[OSD([subQ0])],"isStart":false}),makeQuery(id+"F3.opExtrude","SWEPT_FACE",FACE,{"disambiguationData":[OSD([subQ0])]})],"blendedInto":[makeQuery(id+"F3.opExtrude","SWEPT_FACE",FACE,{"disambiguationData":[OSD([subQ0])]})]});}
            var Q7;
            {var subQ0=sQuery(id+"F2.wireOp",EDGE,"E6");var subQ1=makeQuery(id+"F2.imprint","IMPRINT",EDGE,{"disambiguationData":[TD([[makeQuery(id+"F2.imprint","INTERSECT",VERTEX,{"derivedFrom":[subQ0,sQuery(id+"F2.wireOp",EDGE,"E10.3.2")]}),-1.0]])],"derivedFrom":subQ0});Q7=makeQuery(id+"F4.opChamfer","BLEND_EDGE",EDGE,{"blendedFrom":[makeQuery(id+"F3.opExtrude","CAP_EDGE",EDGE,{"disambiguationData":[OSD([subQ0]),TDD([subQ1])],"isStart":false}),makeQuery(id+"F3.opExtrude","SWEPT_FACE",FACE,{"disambiguationData":[OSD([subQ0]),TDD([subQ1])]})],"blendedInto":[makeQuery(id+"F3.opExtrude","SWEPT_FACE",FACE,{"disambiguationData":[OSD([subQ0]),TDD([subQ1])]})]});}
            var Q8;
            {var subQ0=sQuery(id+"F2.wireOp",EDGE,"E10.3.1");Q8=makeQuery(id+"F4.opChamfer","BLEND_EDGE",EDGE,{"blendedFrom":[makeQuery(id+"F3.opExtrude","CAP_EDGE",EDGE,{"disambiguationData":[OSD([subQ0])],"isStart":false}),makeQuery(id+"F3.opExtrude","SWEPT_FACE",FACE,{"disambiguationData":[OSD([subQ0])]})],"blendedInto":[makeQuery(id+"F3.opExtrude","SWEPT_FACE",FACE,{"disambiguationData":[OSD([subQ0])]})]});}
            var Q9;
            {var subQ0=sQuery(id+"F2.wireOp",EDGE,"E6");var subQ1=makeQuery(id+"F2.imprint","IMPRINT",EDGE,{"disambiguationData":[TD([[makeQuery(id+"F2.imprint","INTERSECT",VERTEX,{"derivedFrom":[subQ0,sQuery(id+"F2.wireOp",EDGE,"E10.2.2")]}),-1.0]])],"derivedFrom":subQ0});Q9=makeQuery(id+"F4.opChamfer","BLEND_EDGE",EDGE,{"blendedFrom":[makeQuery(id+"F3.opExtrude","CAP_EDGE",EDGE,{"disambiguationData":[OSD([subQ0]),TDD([subQ1])],"isStart":false}),makeQuery(id+"F3.opExtrude","SWEPT_FACE",FACE,{"disambiguationData":[OSD([subQ0]),TDD([subQ1])]})],"blendedInto":[makeQuery(id+"F3.opExtrude","SWEPT_FACE",FACE,{"disambiguationData":[OSD([subQ0]),TDD([subQ1])]})]});}
            fillet(context, id + "F7", {"entities" : qUnion([Q0, Q1, Q2, Q3, Q4, Q5, Q6, Q7, Q8, Q9]), "radius" : 2 * mm, "tangentPropagation" : true, "allowEdgeOverflow" : false});
        }
        {
            var Q0;
            Q0=makeQuery(id+"F1.opExtrude","CAP_EDGE",EDGE,{"disambiguationData":[OSD([sQuery(id+"F0.wireOp",EDGE,"E0.top")])],"isStart":true});
            var Q1;
            Q1=makeQuery(id+"F1.opExtrude","CAP_EDGE",EDGE,{"disambiguationData":[OSD([sQuery(id+"F0.wireOp",EDGE,"E0.right")])],"isStart":true});
            var Q2;
            Q2=makeQuery(id+"F1.opExtrude","CAP_EDGE",EDGE,{"disambiguationData":[OSD([sQuery(id+"F0.wireOp",EDGE,"E0.bottom")])],"isStart":true});
            var Q3;
            Q3=makeQuery(id+"F1.opExtrude","CAP_EDGE",EDGE,{"disambiguationData":[OSD([sQuery(id+"F0.wireOp",EDGE,"E0.left")])],"isStart":true});
            fillet(context, id + "F8", {"entities" : qUnion([Q0, Q1, Q2, Q3]), "radius" : 1 * mm, "tangentPropagation" : true, "allowEdgeOverflow" : false});
        }
        {
            var Q0;
            Q0=makeQuery(id+"F0.imprint","IMPRINT",FACE,{"disambiguationData":[TD([[makeQuery(id+"F0.imprint","IMPRINT",EDGE,{"derivedFrom":sQuery(id+"F0.wireOp",EDGE,"E0.bottom")}),-1.0]])]});
            extrude(context, id + "F9", {"entities" : qUnion([Q0]), "operationType" : NewBodyOperationType.REMOVE, "depth" : 18 * mm, "offsetDistance" : 25 * mm});
        }
    });
